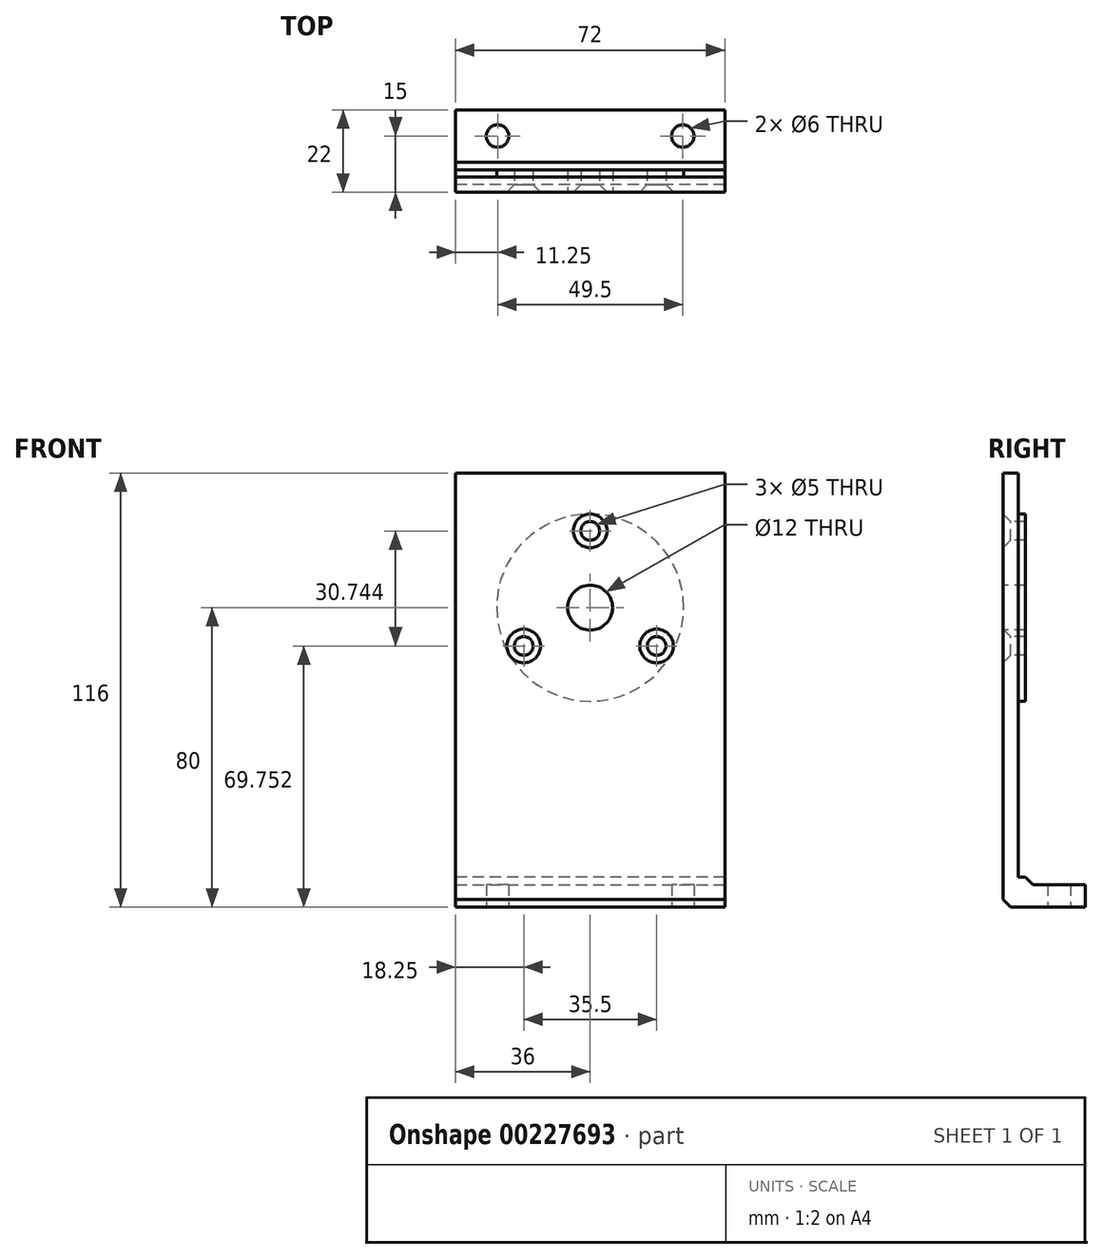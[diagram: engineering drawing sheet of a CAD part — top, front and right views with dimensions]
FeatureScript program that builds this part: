
annotation { "Feature Type Name" : "Feature", "Feature Type Description" : "" }
export const myFeature = defineFeature(function(context is Context, id is Id, definition is map)
    precondition{}
    {
        {
            var Q0;
            Q0=qCreatedBy(makeId("Front.planeOp"),FACE);
            var sketch = newSketch(context, id + "F0", { "sketchPlane" : qUnion([Q0])});
            skLineSegment(sketch, "E0.bottom", {"start": v(-36, 0) * mm, "end": v(36, 0) * mm});
            skLineSegment(sketch, "E0.top", {"start": v(-36, 116) * mm, "end": v(36, 116) * mm});
            skLineSegment(sketch, "E0.left", {"start": v(-36, 0) * mm, "end": v(-36, 116) * mm});
            skLineSegment(sketch, "E0.right", {"start": v(36, 0) * mm, "end": v(36, 116) * mm});
            skCircle(sketch, "E1", {"center": v(0, 80) * mm, "radius": 6 * mm});
            skCircle(sketch, "E2", {"center": v(0, 80) * mm, "radius": 20.5 * mm, "construction": true});
            skLineSegment(sketch, "E3.0", {"start": v(17.75, 69.75) * mm, "end": v(-17.75, 69.75) * mm, "construction": true});
            skLineSegment(sketch, "E3.1", {"start": v(-17.75, 69.75) * mm, "end": v(0, 100.5) * mm, "construction": true});
            skLineSegment(sketch, "E3.2", {"start": v(0, 100.5) * mm, "end": v(17.75, 69.75) * mm, "construction": true});
            skCircle(sketch, "E4", {"center": v(0, 100.5) * mm, "radius": 2.5 * mm});
            skCircle(sketch, "E5", {"center": v(17.75, 69.75) * mm, "radius": 2.5 * mm});
            skCircle(sketch, "E6", {"center": v(-17.75, 69.75) * mm, "radius": 2.5 * mm});
            skSolve(sketch);
        }
        {
            var Q0;
            Q0=qCreatedBy(makeId("Top.planeOp"),FACE);
            var sketch = newSketch(context, id + "F1", { "sketchPlane" : qUnion([Q0])});
            skLineSegment(sketch, "E7.0", {"start": v(-36, 0) * mm, "end": v(36, 0) * mm});
            skLineSegment(sketch, "E8", {"start": v(-36, 0) * mm, "end": v(-36, 22) * mm});
            skLineSegment(sketch, "E9", {"start": v(-36, 22) * mm, "end": v(36, 22) * mm});
            skLineSegment(sketch, "E10", {"start": v(36, 22) * mm, "end": v(36, 0) * mm});
            skCircle(sketch, "E11", {"center": v(-24.75, 15) * mm, "radius": 3 * mm});
            skCircle(sketch, "E12", {"center": v(24.75, 15) * mm, "radius": 3 * mm});
            skSolve(sketch);
        }
        {
            var Q0;
            Q0=makeQuery(id+"F0.imprint","IMPRINT",FACE,{"disambiguationData":[TD([[makeQuery(id+"F0.imprint","IMPRINT",EDGE,{"derivedFrom":sQuery(id+"F0.wireOp",EDGE,"E0.bottom")}),1.0]])]});
            extrude(context, id + "F2", {"entities" : qUnion([Q0]), "oppositeDirection" : true, "depth" : 6 * mm});
        }
        {
            var Q0;
            Q0=makeQuery(id+"F1.imprint","IMPRINT",FACE,{"disambiguationData":[TD([[makeQuery(id+"F1.imprint","IMPRINT",EDGE,{"derivedFrom":sQuery(id+"F1.wireOp",EDGE,"E7.0")}),1.0]])]});
            extrude(context, id + "F3", {"entities" : qUnion([Q0]), "operationType" : NewBodyOperationType.ADD, "depth" : 6 * mm});
        }
        {
            var Q0;
            Q0=makeQuery(id+"F3.boolean.opBoolean","INTERSECT",EDGE,{"derivedFrom":[makeQuery(id+"F2.opExtrude","CAP_FACE",FACE,{"disambiguationData":[OSD([sQuery(id+"F0.wireOp",EDGE,"E0.bottom"),sQuery(id+"F0.wireOp",EDGE,"E0.top"),sQuery(id+"F0.wireOp",EDGE,"E0.left"),sQuery(id+"F0.wireOp",EDGE,"E0.right"),sQuery(id+"F0.wireOp",EDGE,"E1"),sQuery(id+"F0.wireOp",EDGE,"E4"),sQuery(id+"F0.wireOp",EDGE,"E5"),sQuery(id+"F0.wireOp",EDGE,"E6")])],"isStart":false}),makeQuery(id+"F3.opExtrude","CAP_FACE",FACE,{"disambiguationData":[OSD([sQuery(id+"F1.wireOp",EDGE,"E7.0"),sQuery(id+"F1.wireOp",EDGE,"E8"),sQuery(id+"F1.wireOp",EDGE,"E9"),sQuery(id+"F1.wireOp",EDGE,"E10"),sQuery(id+"F1.wireOp",EDGE,"E11"),sQuery(id+"F1.wireOp",EDGE,"E12")])],"isStart":false})]});
            chamfer(context, id + "F4", {"entities" : qUnion([Q0]), "width" : 2 * mm, "tangentPropagation" : true});
        }
        {
            var Q0;
            Q0=makeQuery(id+"F2.opExtrude","CAP_EDGE",EDGE,{"disambiguationData":[OSD([sQuery(id+"F0.wireOp",EDGE,"E0.bottom")])],"isStart":true});
            chamfer(context, id + "F5", {"entities" : qUnion([Q0]), "width" : 2 * mm, "tangentPropagation" : true});
        }
        {
            var Q0;
            Q0=makeQuery(id+"F2.opExtrude","CAP_EDGE",EDGE,{"disambiguationData":[OSD([sQuery(id+"F0.wireOp",EDGE,"E4")])],"isStart":true});
            var Q1;
            Q1=makeQuery(id+"F2.opExtrude","CAP_EDGE",EDGE,{"disambiguationData":[OSD([sQuery(id+"F0.wireOp",EDGE,"E6")])],"isStart":true});
            var Q2;
            Q2=makeQuery(id+"F2.opExtrude","CAP_EDGE",EDGE,{"disambiguationData":[OSD([sQuery(id+"F0.wireOp",EDGE,"E5")])],"isStart":true});
            chamfer(context, id + "F6", {"entities" : qUnion([Q0, Q1, Q2]), "width" : 2 * mm, "tangentPropagation" : true});
        }
        {
            var Q0;
            Q0=makeQuery(id+"F2.opExtrude","CAP_FACE",FACE,{"disambiguationData":[OSD([sQuery(id+"F0.wireOp",EDGE,"E0.bottom"),sQuery(id+"F0.wireOp",EDGE,"E0.top"),sQuery(id+"F0.wireOp",EDGE,"E0.left"),sQuery(id+"F0.wireOp",EDGE,"E0.right"),sQuery(id+"F0.wireOp",EDGE,"E1"),sQuery(id+"F0.wireOp",EDGE,"E4"),sQuery(id+"F0.wireOp",EDGE,"E5"),sQuery(id+"F0.wireOp",EDGE,"E6")])],"isStart":false});
            var sketch = newSketch(context, id + "F7", { "sketchPlane" : qUnion([Q0])});
            skCircle(sketch, "E13.0", {"center": v(0, 80) * mm, "radius": 25 * mm});
            skSolve(sketch);
        }
        {
            var Q0;
            Q0=makeQuery(id+"F7.imprint","IMPRINT",FACE,{"disambiguationData":[TD([[makeQuery(id+"F7.imprint","IMPRINT",EDGE,{"derivedFrom":sQuery(id+"F7.wireOp",EDGE,"E13.0")}),-1.0]])]});
            extrude(context, id + "F8", {"entities" : qUnion([Q0]), "operationType" : NewBodyOperationType.REMOVE, "oppositeDirection" : true, "depth" : 2 * mm});
        }
    });
